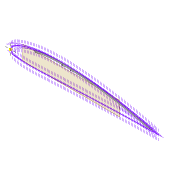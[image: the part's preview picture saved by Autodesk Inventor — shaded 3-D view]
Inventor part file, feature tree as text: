
AUTODESK INVENTOR PART (.ipt)
format: ipt  version: 2022 (Build 260153000, 153)  size: 467,968 bytes
history: native  units: mm
features: sketch x9, projected_geometry x8, extrude x7, shell x1, plane x1, chamfer x1
ambient origin geometry x8: Origin, YZ Plane, XZ Plane, XY Plane, X Axis, Y Axis, Z Axis, Center Point
bodies: Solid1 (feature_tree)
feature tree (27):
  extrude  "Extrusion1"  Depth=4.0mm
  shell  "Shell1"  Thickness=2.0mm
  extrude  "Extrusion8"  Depth=5.9mm
  extrude  "Extrusion3"  Depth=10.0mm TaperAngle=0.0deg
  extrude  "Extrusion4"  Depth=5.0mm
  extrude  "Extrusion5"  Depth=2.5mm
  plane  "Work Plane2"
  extrude  "Extrusion9"  Depth=5.0mm
  chamfer  "Chamfer1"  Distance=2.0mm
  extrude  "Extrusion11"  Depth=20.0mm
  sketch  "Sketch30"  dims[d62=75.0mm]
  sketch  "Sketch31"  dims[d63=5.0mm d64=2.0mm d65=0.0mm d66=2.5mm d67=12.0mm d68=75.0mm d69=20.0mm d70=0.5mm d71=10.0mm d72=0.0mm d75=3.0mm d77=3.0mm d78=2.0mm d79=45.0deg d81=1.0mm d83=0.0mm d84=1.0mm d85=1.0mm d86=1.0mm d87=1.0mm d88=10.0mm d89=0.0mm]
  sketch  "Sketch3"  dims[d0=2.0mm d1=0.0mm d2=4.0mm d7=2.0mm]
  sketch  "Sketch8"  dims[d8=2.0mm d9=5.9mm]
  sketch  "Sketch9"  dims[d13=10.0mm d14=0.0mm d16=10.0mm d17=0.0mm]
  sketch  "Sketch10"  dims[d22=2.0mm d23=0.0mm d32=5.0mm]
  projected_geometry  "Projected Loop4"
  projected_geometry  "Projected Loop10"
  sketch  "Sketch24"  dims[d34=1.6mm d35=2.5mm]
  projected_geometry  "Projected Loop11"
  projected_geometry  "Projected Loop12"
  sketch  "Sketch26"  dims[d37=5.0mm d38=1.6mm]
  projected_geometry  "Projected Loop13"
  sketch  "Sketch29"  dims[d40=2.5mm]
  projected_geometry  "Project Cut Edges2"
  projected_geometry  "Project Cut Edges3"
  projected_geometry  "Project Cut Edges4"
